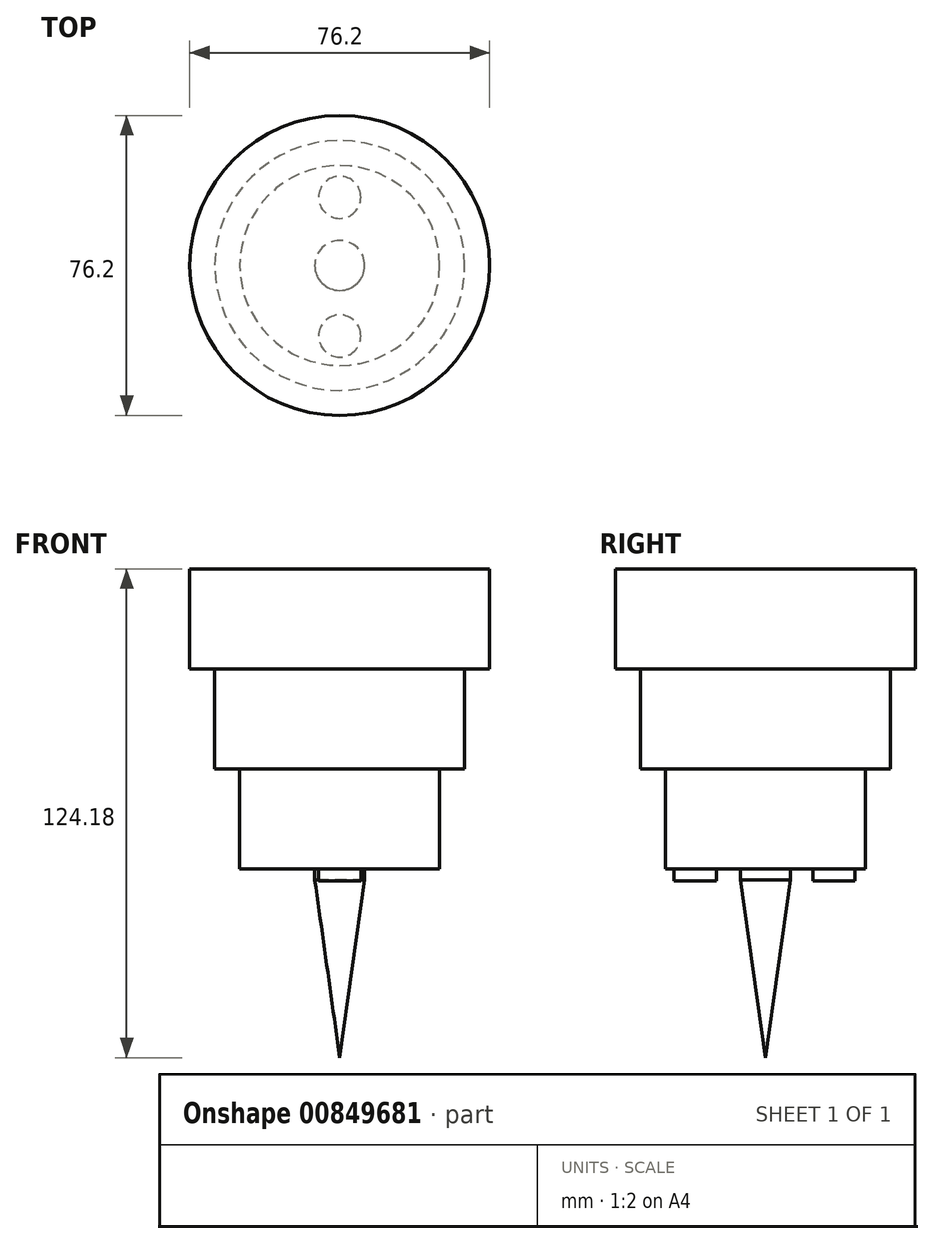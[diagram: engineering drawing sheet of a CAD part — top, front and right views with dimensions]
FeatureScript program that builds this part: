
annotation { "Feature Type Name" : "Feature", "Feature Type Description" : "" }
export const myFeature = defineFeature(function(context is Context, id is Id, definition is map)
    precondition{}
    {
        {
            var Q0;
            Q0=qCreatedBy(makeId("Top.planeOp"),FACE);
            var sketch = newSketch(context, id + "F0", { "sketchPlane" : qUnion([Q0])});
            skCircle(sketch, "E0", {"center": v(0, 0) * mm, "radius": 38.1 * mm});
            skSolve(sketch);
        }
        {
            var Q0;
            Q0 = qSketchRegion(id + "F0", true);
            extrude(context, id + "F1", {"entities" : qUnion([Q0]), "depth" : 25.4 * mm, "offsetDistance" : 25.4 * mm});
        }
        {
            var Q0;
            Q0=qCreatedBy(makeId("Top.planeOp"),FACE);
            var sketch = newSketch(context, id + "F2", { "sketchPlane" : qUnion([Q0])});
            skCircle(sketch, "E1", {"center": v(0, 0) * mm, "radius": 31.75 * mm});
            skSolve(sketch);
        }
        {
            var Q0;
            Q0 = qSketchRegion(id + "F2", true);
            extrude(context, id + "F3", {"entities" : qUnion([Q0]), "operationType" : NewBodyOperationType.ADD, "oppositeDirection" : true, "depth" : 25.4 * mm, "offsetDistance" : 25.4 * mm});
        }
        {
            var Q0;
            Q0=qCreatedBy(makeId("Top.planeOp"),FACE);
            var sketch = newSketch(context, id + "F4", { "sketchPlane" : qUnion([Q0])});
            skCircle(sketch, "E2", {"center": v(0, 0) * mm, "radius": 25.4 * mm});
            skSolve(sketch);
        }
        {
            var Q0;
            Q0 = qSketchRegion(id + "F4", true);
            extrude(context, id + "F5", {"entities" : qUnion([Q0]), "operationType" : NewBodyOperationType.ADD, "oppositeDirection" : true, "depth" : 50.8 * mm, "offsetDistance" : 25.4 * mm});
        }
        {
            var Q0;
            Q0=qCreatedBy(makeId("Top.planeOp"),FACE);
            var sketch = newSketch(context, id + "F6", { "sketchPlane" : qUnion([Q0])});
            skCircle(sketch, "E3", {"center": v(0, 0) * mm, "radius": 6.35 * mm});
            skSolve(sketch);
        }
        {
            var Q0;
            Q0 = qSketchRegion(id + "F6", true);
            extrude(context, id + "F7", {"entities" : qUnion([Q0]), "operationType" : NewBodyOperationType.ADD, "oppositeDirection" : true, "depth" : 53.6 * mm, "offsetDistance" : 25.4 * mm});
        }
        {
            var Q0;
            Q0=makeQuery(id+"F7.opExtrude","CAP_FACE",FACE,{"disambiguationData":[OSD([sQuery(id+"F6.wireOp",EDGE,"E3")])],"isStart":false});
            extrude(context, id + "F8", {"entities" : qUnion([Q0]), "operationType" : NewBodyOperationType.ADD, "depth" : 78.23 * mm, "offsetDistance" : 25.4 * mm, "hasDraft" : true, "draftAngle" : 8 * degree, "draftPullDirection" : true});
        }
        {
            var Q0;
            Q0=qCreatedBy(makeId("Top.planeOp"),FACE);
            var sketch = newSketch(context, id + "F9", { "sketchPlane" : qUnion([Q0])});
            skPoint(sketch, "E4", {"position": v(0, -17.92) * mm});
            skCircle(sketch, "E5", {"center": v(0, -17.92) * mm, "radius": 5.36 * mm});
            skSolve(sketch);
        }
        {
            var Q0;
            Q0=qCreatedBy(makeId("Top.planeOp"),FACE);
            var sketch = newSketch(context, id + "F10", { "sketchPlane" : qUnion([Q0])});
            skPoint(sketch, "E6", {"position": v(0, 17.3) * mm});
            skCircle(sketch, "E7", {"center": v(0, 17.3) * mm, "radius": 5.36 * mm});
            skSolve(sketch);
        }
        {
            var Q0;
            Q0 = qSketchRegion(id + "F10", true);
            extrude(context, id + "F11", {"entities" : qUnion([Q0]), "operationType" : NewBodyOperationType.ADD, "oppositeDirection" : true, "depth" : 53.85 * mm, "offsetDistance" : 25.4 * mm});
        }
        {
            var Q0;
            Q0 = qSketchRegion(id + "F9", true);
            extrude(context, id + "F12", {"entities" : qUnion([Q0]), "operationType" : NewBodyOperationType.ADD, "oppositeDirection" : true, "depth" : 53.85 * mm, "offsetDistance" : 25.4 * mm});
        }
    });
